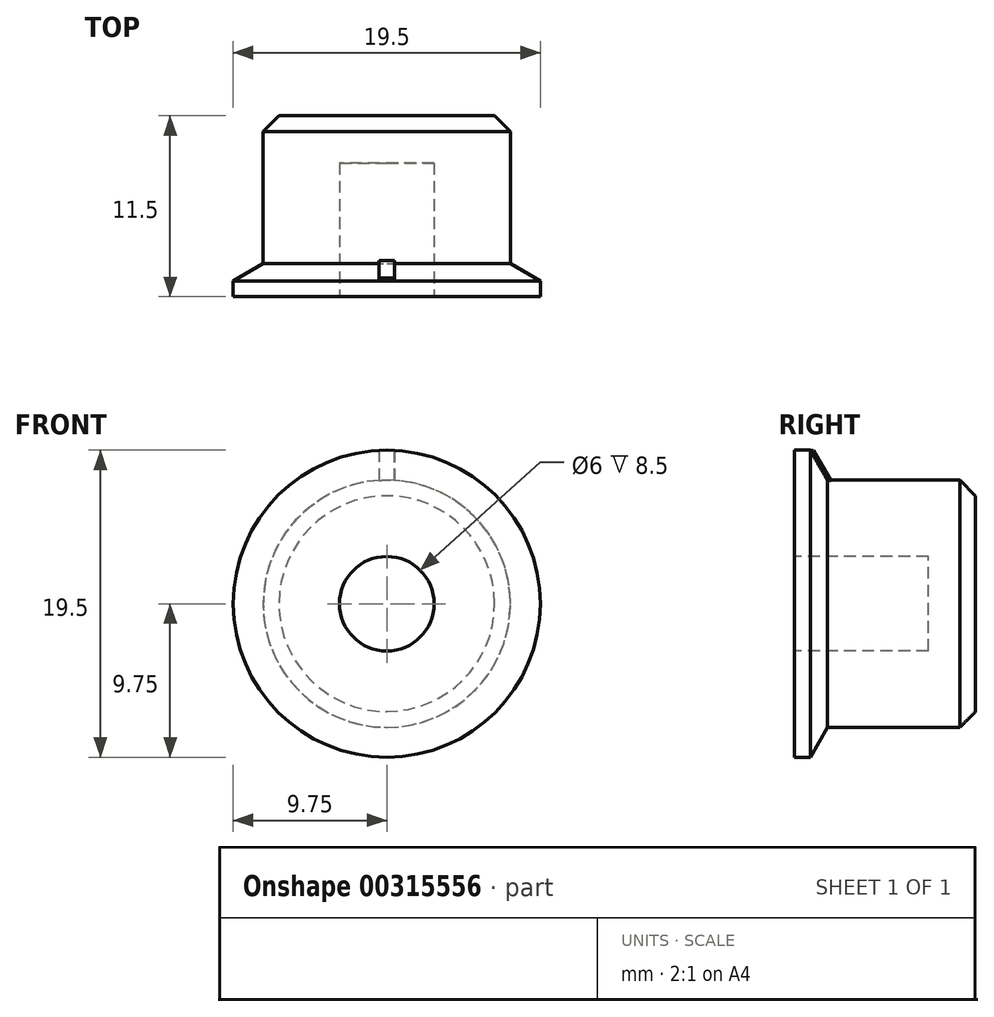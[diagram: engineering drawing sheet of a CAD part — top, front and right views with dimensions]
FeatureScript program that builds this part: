
annotation { "Feature Type Name" : "Feature", "Feature Type Description" : "" }
export const myFeature = defineFeature(function(context is Context, id is Id, definition is map)
    precondition{}
    {
        {
            var Q0;
            Q0=qCreatedBy(makeId("Top.planeOp"),FACE);
            var sketch = newSketch(context, id + "F0", { "sketchPlane" : qUnion([Q0])});
            skLineSegment(sketch, "E0", {"start": v(0, 11.5) * mm, "end": v(-7.85, 11.5) * mm});
            skLineSegment(sketch, "E1", {"start": v(-7.85, 11.5) * mm, "end": v(-7.85, 2.1) * mm});
            skLineSegment(sketch, "E2", {"start": v(-7.85, 2.1) * mm, "end": v(-9.75, 1) * mm});
            skLineSegment(sketch, "E3", {"start": v(-9.75, 1) * mm, "end": v(-9.75, 0) * mm});
            skLineSegment(sketch, "E4", {"start": v(-9.75, 0) * mm, "end": v(-3, 0) * mm});
            skLineSegment(sketch, "E5", {"start": v(-3, 0) * mm, "end": v(-3, 8.5) * mm});
            skLineSegment(sketch, "E6", {"start": v(-3, 8.5) * mm, "end": v(0, 8.5) * mm});
            skLineSegment(sketch, "E7", {"start": v(0, 8.5) * mm, "end": v(0, 11.5) * mm});
            skLineSegment(sketch, "E8", {"start": v(0, 0) * mm, "end": v(0, 28.18) * mm, "construction": true});
            skSolve(sketch);
        }
        {
            var Q0;
            Q0=qSketchRegion(id+"F0",true);
            var Q1;
            Q1=sQuery(id+"F0.wireOp",EDGE,"E8");
            revolve(context, id + "F1", {"entities" : qUnion([Q0]), "axis" : qUnion([Q1]), "revolveType" : RevolveType.FULL});
        }
        {
            var Q0;
            Q0=makeQuery(id+"F1.opRevolve","SWEPT_FACE",FACE,{"disambiguationData":[OSD([sQuery(id+"F0.wireOp",EDGE,"E4")])]});
            var sketch = newSketch(context, id + "F2", { "sketchPlane" : qUnion([Q0])});
            skLineSegment(sketch, "E9.bottom", {"start": v(0.5, 9.74) * mm, "end": v(-0.5, 9.74) * mm});
            skLineSegment(sketch, "E9.top", {"start": v(0.5, 6.74) * mm, "end": v(-0.5, 6.74) * mm});
            skLineSegment(sketch, "E9.left", {"start": v(0.5, 9.74) * mm, "end": v(0.5, 6.74) * mm});
            skLineSegment(sketch, "E9.right", {"start": v(-0.5, 9.74) * mm, "end": v(-0.5, 6.74) * mm});
            skPoint(sketch, "E9.middle", {"position": v(0, 8.24) * mm});
            skSolve(sketch);
        }
        {
            var Q0;
            Q0=qSketchRegion(id+"F2",true);
            extrude(context, id + "F3", {"entities" : qUnion([Q0]), "operationType" : NewBodyOperationType.ADD, "oppositeDirection" : true, "depth" : 3 * mm});
        }
        {
            var Q0;
            Q0=makeQuery(id+"F3.opExtrude","CAP_EDGE",EDGE,{"disambiguationData":[OSD([sQuery(id+"F2.wireOp",EDGE,"E9.bottom")])],"isStart":false});
            chamfer(context, id + "F4", {"entities" : qUnion([Q0]), "chamferType" : ChamferType.OFFSET_ANGLE, "width" : 1.8 * mm, "oppositeDirection" : false, "angle" : 60 * degree, "tangentPropagation" : true});
        }
        {
            var Q0;
            Q0=makeQuery(id+"F1.opRevolve","SWEPT_EDGE",EDGE,{"disambiguationData":[OSD([sQuery(id+"F0.wireOp",EDGE,"E0"),sQuery(id+"F0.wireOp",EDGE,"E1")])]});
            chamfer(context, id + "F5", {"entities" : qUnion([Q0]), "width" : 1 * mm, "tangentPropagation" : true});
        }
    });
